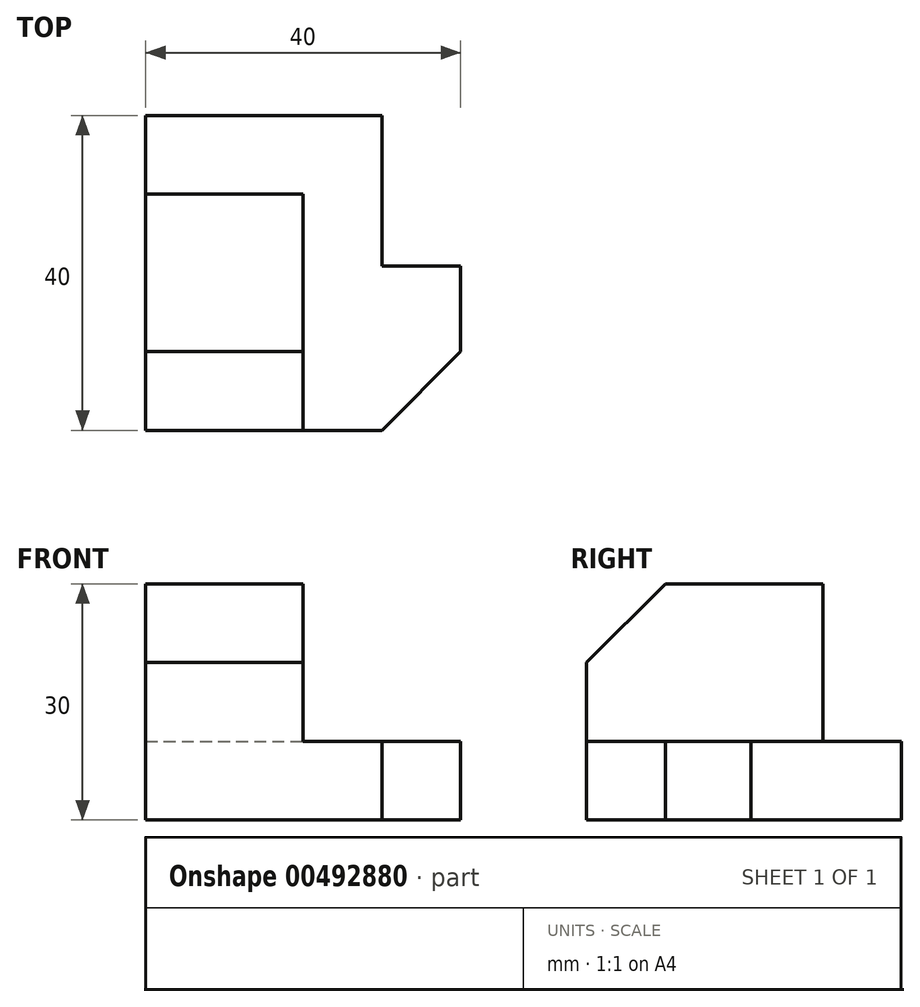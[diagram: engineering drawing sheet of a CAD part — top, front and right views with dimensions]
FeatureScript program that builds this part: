
annotation { "Feature Type Name" : "Feature", "Feature Type Description" : "" }
export const myFeature = defineFeature(function(context is Context, id is Id, definition is map)
    precondition{}
    {
        {
            var Q0;
            Q0=qCreatedBy(makeId("Top.planeOp"),FACE);
            var sketch = newSketch(context, id + "F0", { "sketchPlane" : qUnion([Q0])});
            skLineSegment(sketch, "E0", {"start": v(0, 0) * mm, "end": v(0, 40) * mm});
            skLineSegment(sketch, "E1", {"start": v(0, 40) * mm, "end": v(30, 40) * mm});
            skLineSegment(sketch, "E2", {"start": v(30, 40) * mm, "end": v(30, 20.9) * mm});
            skLineSegment(sketch, "E3", {"start": v(30, 20.9) * mm, "end": v(40, 20.9) * mm});
            skLineSegment(sketch, "E4", {"start": v(40, 20.9) * mm, "end": v(40, 10) * mm});
            skLineSegment(sketch, "E5", {"start": v(40, 10) * mm, "end": v(30, 0) * mm});
            skLineSegment(sketch, "E6", {"start": v(30, 0) * mm, "end": v(0, 0) * mm});
            skSolve(sketch);
        }
        {
            var Q0;
            Q0=makeQuery(id+"F0.imprint","IMPRINT",FACE,{"disambiguationData":[TD([[makeQuery(id+"F0.imprint","IMPRINT",EDGE,{"derivedFrom":sQuery(id+"F0.wireOp",EDGE,"E0")}),-1.0]])]});
            extrude(context, id + "F1", {"entities" : qUnion([Q0]), "depth" : 10 * mm});
        }
        {
            var Q0;
            Q0=makeQuery(id+"F1.opExtrude","CAP_FACE",FACE,{"disambiguationData":[OSD([sQuery(id+"F0.wireOp",EDGE,"E0"),sQuery(id+"F0.wireOp",EDGE,"E1"),sQuery(id+"F0.wireOp",EDGE,"E2"),sQuery(id+"F0.wireOp",EDGE,"E3"),sQuery(id+"F0.wireOp",EDGE,"E4"),sQuery(id+"F0.wireOp",EDGE,"E5"),sQuery(id+"F0.wireOp",EDGE,"E6")])],"isStart":false});
            var sketch = newSketch(context, id + "F2", { "sketchPlane" : qUnion([Q0])});
            skLineSegment(sketch, "E7", {"start": v(0, 30) * mm, "end": v(20, 30) * mm});
            skLineSegment(sketch, "E8", {"start": v(20, 30) * mm, "end": v(20, 0) * mm});
            skLineSegment(sketch, "E9", {"start": v(20, 0) * mm, "end": v(0, 0) * mm});
            skLineSegment(sketch, "E10", {"start": v(0, 0) * mm, "end": v(0, 30) * mm});
            skSolve(sketch);
        }
        {
            var Q0;
            Q0=makeQuery(id+"F2.imprint","IMPRINT",FACE,{"disambiguationData":[TD([[makeQuery(id+"F2.imprint","IMPRINT",EDGE,{"derivedFrom":sQuery(id+"F2.wireOp",EDGE,"E7")}),-1.0]])]});
            extrude(context, id + "F3", {"entities" : qUnion([Q0]), "operationType" : NewBodyOperationType.ADD, "depth" : 20 * mm});
        }
        {
            var Q0;
            Q0=makeQuery(id+"F3.opExtrude","CAP_EDGE",EDGE,{"disambiguationData":[OSD([sQuery(id+"F2.wireOp",EDGE,"E9")])],"isStart":false});
            chamfer(context, id + "F4", {"entities" : qUnion([Q0]), "chamferType" : ChamferType.OFFSET_ANGLE, "width" : 10 * mm, "oppositeDirection" : false, "angle" : 45 * degree, "tangentPropagation" : true});
        }
    });
